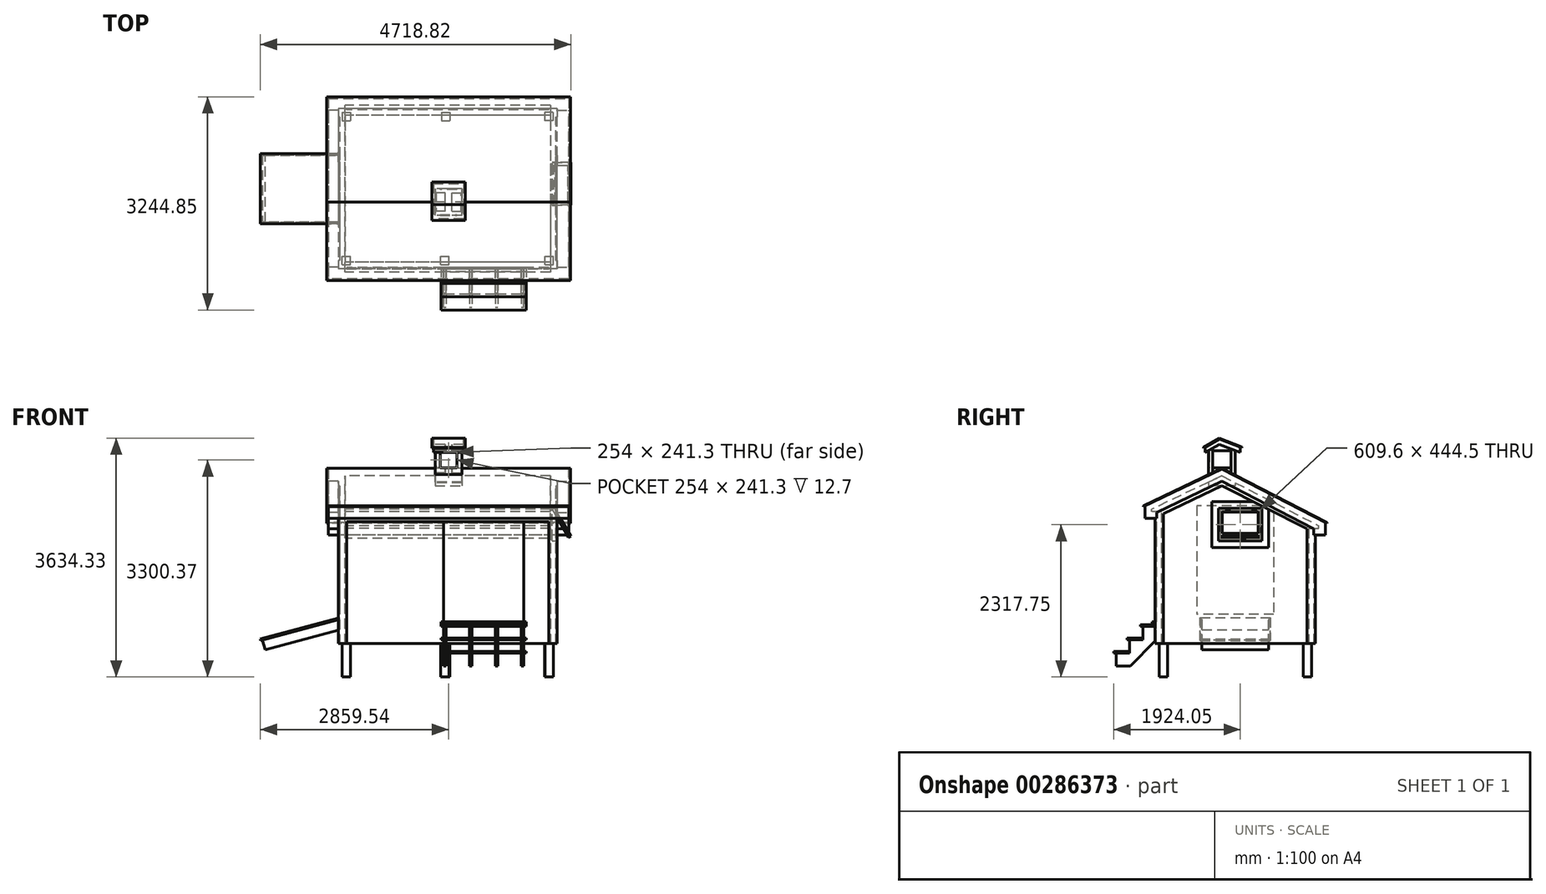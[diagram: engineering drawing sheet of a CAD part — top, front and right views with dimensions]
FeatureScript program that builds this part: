
annotation { "Feature Type Name" : "Feature", "Feature Type Description" : "" }
export const myFeature = defineFeature(function(context is Context, id is Id, definition is map)
    precondition{}
    {
        {
            var Q0;
            Q0=qCreatedBy(makeId("Right.planeOp"),FACE);
            var sketch = newSketch(context, id + "F0", { "sketchPlane" : qUnion([Q0])});
            skLineSegment(sketch, "E0", {"start": v(-152.4, 1905) * mm, "end": v(-152.4, 2108.2) * mm});
            skLineSegment(sketch, "E1", {"start": v(-152.4, 2108.2) * mm, "end": v(1016, 2667) * mm});
            skLineSegment(sketch, "E2", {"start": v(1016, 2667) * mm, "end": v(2590.8, 1854.2) * mm});
            skLineSegment(sketch, "E3", {"start": v(2590.8, 1854.2) * mm, "end": v(2590.8, 1651) * mm});
            skLineSegment(sketch, "E4", {"start": v(2590.8, 1651) * mm, "end": v(2438.4, 1651) * mm});
            skLineSegment(sketch, "E5", {"start": v(2438.4, 1651) * mm, "end": v(2438.4, 0) * mm});
            skLineSegment(sketch, "E6", {"start": v(2438.4, 0) * mm, "end": v(0, 0) * mm});
            skLineSegment(sketch, "E7", {"start": v(0, 0) * mm, "end": v(0, 1905) * mm});
            skLineSegment(sketch, "E8", {"start": v(0, 1905) * mm, "end": v(-152.4, 1905) * mm});
            skSolve(sketch);
        }
        {
            var Q0;
            Q0 = qSketchRegion(id + "F0", true);
            extrude(context, id + "F1", {"entities" : qUnion([Q0]), "depth" : 3657.6 * mm});
        }
        {
            var Q0;
            Q0=makeQuery(id+"F1.opExtrude","CAP_FACE",FACE,{"disambiguationData":[OSD([sQuery(id+"F0.wireOp",EDGE,"E0"),sQuery(id+"F0.wireOp",EDGE,"E1"),sQuery(id+"F0.wireOp",EDGE,"E2"),sQuery(id+"F0.wireOp",EDGE,"E3"),sQuery(id+"F0.wireOp",EDGE,"E4"),sQuery(id+"F0.wireOp",EDGE,"E5"),sQuery(id+"F0.wireOp",EDGE,"E6"),sQuery(id+"F0.wireOp",EDGE,"E7"),sQuery(id+"F0.wireOp",EDGE,"E8")])],"isStart":false});
            var sketch = newSketch(context, id + "F2", { "sketchPlane" : qUnion([Q0])});
            skLineSegment(sketch, "E9", {"start": v(0, 1905) * mm, "end": v(25.4, 1905) * mm});
            skLineSegment(sketch, "E10", {"start": v(25.4, 1905) * mm, "end": v(25.4, 1996.15) * mm});
            skLineSegment(sketch, "E11", {"start": v(25.4, 1996.15) * mm, "end": v(1016, 2469.91) * mm});
            skLineSegment(sketch, "E12", {"start": v(1016, 2469.91) * mm, "end": v(2413, 1748.88) * mm});
            skLineSegment(sketch, "E13", {"start": v(2413, 1748.88) * mm, "end": v(2413, 1651) * mm});
            skLineSegment(sketch, "E14", {"start": v(2413, 1651) * mm, "end": v(2438.4, 1651) * mm});
            skSolve(sketch);
        }
        {
            var Q0;
            Q0=makeQuery(id+"F2.imprint","IMPRINT",FACE,{"disambiguationData":[TD([[makeQuery(id+"F2.imprint","IMPRINT",EDGE,{"derivedFrom":sQuery(id+"F2.wireOp",EDGE,"E9")}),-1.0]])]});
            extrude(context, id + "F3", {"entities" : qUnion([Q0]), "operationType" : NewBodyOperationType.REMOVE, "oppositeDirection" : true, "depth" : 177.8 * mm});
        }
        {
            var Q0;
            Q0=makeQuery(id+"F1.opExtrude","CAP_FACE",FACE,{"disambiguationData":[OSD([sQuery(id+"F0.wireOp",EDGE,"E0"),sQuery(id+"F0.wireOp",EDGE,"E1"),sQuery(id+"F0.wireOp",EDGE,"E2"),sQuery(id+"F0.wireOp",EDGE,"E3"),sQuery(id+"F0.wireOp",EDGE,"E4"),sQuery(id+"F0.wireOp",EDGE,"E5"),sQuery(id+"F0.wireOp",EDGE,"E6"),sQuery(id+"F0.wireOp",EDGE,"E7"),sQuery(id+"F0.wireOp",EDGE,"E8")])],"isStart":true});
            var sketch = newSketch(context, id + "F4", { "sketchPlane" : qUnion([Q0])});
            skLineSegment(sketch, "E15.0.0", {"start": v(-2438.4, 1651) * mm, "end": v(-2413, 1651) * mm});
            skLineSegment(sketch, "E15.0.1", {"start": v(-2413, 1651) * mm, "end": v(-2413, 1748.88) * mm});
            skLineSegment(sketch, "E15.0.2", {"start": v(-2413, 1748.88) * mm, "end": v(-1016, 2469.91) * mm});
            skLineSegment(sketch, "E15.0.3", {"start": v(-1016, 2469.91) * mm, "end": v(-25.4, 1996.15) * mm});
            skLineSegment(sketch, "E15.0.4", {"start": v(-25.4, 1996.15) * mm, "end": v(-25.4, 1905) * mm});
            skLineSegment(sketch, "E15.0.5", {"start": v(-25.4, 1905) * mm, "end": v(0, 1905) * mm});
            skLineSegment(sketch, "E15.0.6", {"start": v(0, 1905) * mm, "end": v(0, 0) * mm});
            skLineSegment(sketch, "E15.0.7", {"start": v(0, 0) * mm, "end": v(-2438.4, 0) * mm});
            skLineSegment(sketch, "E15.0.8", {"start": v(-2438.4, 0) * mm, "end": v(-2438.4, 1651) * mm});
            skSolve(sketch);
        }
        {
            var Q0;
            Q0 = qSketchRegion(id + "F4", true);
            extrude(context, id + "F5", {"entities" : qUnion([Q0]), "operationType" : NewBodyOperationType.REMOVE, "oppositeDirection" : true, "depth" : 152.4 * mm});
        }
        {
            var Q0;
            Q0=makeQuery(id+"F1.opExtrude","SWEPT_FACE",FACE,{"disambiguationData":[OSD([sQuery(id+"F0.wireOp",EDGE,"E6")])]});
            shell(context, id + "F6", {"entities" : qUnion([Q0]), "thickness" : 101.6 * mm});
        }
        {
            var Q0;
            Q0=makeQuery(id+"F3.boolean.opBoolean","COPY",FACE,{"derivedFrom":makeQuery(id+"F3.opExtrude","CAP_FACE",FACE,{"disambiguationData":[OSD([sQuery(id+"F0.wireOp",EDGE,"E5"),sQuery(id+"F0.wireOp",EDGE,"E6"),sQuery(id+"F0.wireOp",EDGE,"E7"),sQuery(id+"F2.wireOp",EDGE,"E9"),sQuery(id+"F2.wireOp",EDGE,"E10"),sQuery(id+"F2.wireOp",EDGE,"E11"),sQuery(id+"F2.wireOp",EDGE,"E12"),sQuery(id+"F2.wireOp",EDGE,"E13"),sQuery(id+"F2.wireOp",EDGE,"E14")])],"isStart":false})});
            var sketch = newSketch(context, id + "F7", { "sketchPlane" : qUnion([Q0])});
            skLineSegment(sketch, "E16", {"start": v(127, 0) * mm, "end": v(127, 1974.35) * mm});
            skLineSegment(sketch, "E17", {"start": v(127, 1974.35) * mm, "end": v(1016, 2399.52) * mm});
            skLineSegment(sketch, "E18", {"start": v(1016, 2399.52) * mm, "end": v(2311.4, 1748.88) * mm});
            skLineSegment(sketch, "E19", {"start": v(2311.4, 1748.88) * mm, "end": v(2311.4, 0) * mm});
            skSolve(sketch);
        }
        {
            var Q0;
            {var subQ1=sQuery(id+"F7.wireOp",EDGE,"E16");Q0=makeQuery(id+"F7.imprint","IMPRINT",FACE,{"disambiguationData":[TD([[makeQuery(id+"F7.imprint","IMPRINT",EDGE,{"derivedFrom":subQ1}),-1.0]])]});}
            extrude(context, id + "F8", {"entities" : qUnion([Q0]), "operationType" : NewBodyOperationType.REMOVE, "oppositeDirection" : true, "depth" : 19.05 * mm});
        }
        {
            var Q0;
            Q0=makeQuery(id+"F5.boolean.opBoolean","COPY",FACE,{"derivedFrom":makeQuery(id+"F5.opExtrude","CAP_FACE",FACE,{"disambiguationData":[OSD([sQuery(id+"F4.wireOp",EDGE,"E15.0.0"),sQuery(id+"F4.wireOp",EDGE,"E15.0.1"),sQuery(id+"F4.wireOp",EDGE,"E15.0.2"),sQuery(id+"F4.wireOp",EDGE,"E15.0.3"),sQuery(id+"F4.wireOp",EDGE,"E15.0.4"),sQuery(id+"F4.wireOp",EDGE,"E15.0.5"),sQuery(id+"F4.wireOp",EDGE,"E15.0.6"),sQuery(id+"F4.wireOp",EDGE,"E15.0.7"),sQuery(id+"F4.wireOp",EDGE,"E15.0.8")])],"isStart":false})});
            var sketch = newSketch(context, id + "F9", { "sketchPlane" : qUnion([Q0])});
            skLineSegment(sketch, "E20.0.0", {"start": v(-2311.4, 0) * mm, "end": v(-2311.4, 1748.88) * mm});
            skLineSegment(sketch, "E20.0.1", {"start": v(-2311.4, 1748.88) * mm, "end": v(-1016, 2399.52) * mm});
            skLineSegment(sketch, "E20.0.2", {"start": v(-1016, 2399.52) * mm, "end": v(-127, 1974.35) * mm});
            skLineSegment(sketch, "E20.0.3", {"start": v(-127, 1974.35) * mm, "end": v(-127, 0) * mm});
            skLineSegment(sketch, "E20.0.4", {"start": v(-127, 0) * mm, "end": v(-2311.4, 0) * mm});
            skSolve(sketch);
        }
        {
            var Q0;
            Q0 = qSketchRegion(id + "F9", true);
            extrude(context, id + "F10", {"entities" : qUnion([Q0]), "operationType" : NewBodyOperationType.REMOVE, "oppositeDirection" : true, "depth" : 19.05 * mm});
        }
        {
            var Q0;
            Q0=makeQuery(id+"F1.opExtrude","SWEPT_FACE",FACE,{"disambiguationData":[OSD([sQuery(id+"F0.wireOp",EDGE,"E7")])]});
            var sketch = newSketch(context, id + "F11", { "sketchPlane" : qUnion([Q0])});
            skLineSegment(sketch, "E21", {"start": v(279.4, 0) * mm, "end": v(279.4, 1854.2) * mm});
            skLineSegment(sketch, "E22", {"start": v(279.4, 1854.2) * mm, "end": v(3352.8, 1854.2) * mm});
            skLineSegment(sketch, "E23", {"start": v(3352.8, 1854.2) * mm, "end": v(3352.8, 0) * mm});
            skSolve(sketch);
        }
        {
            var Q0;
            {var subQ0=sQuery(id+"F11.wireOp",EDGE,"E21");Q0=makeQuery(id+"F11.imprint","IMPRINT",FACE,{"disambiguationData":[TD([[makeQuery(id+"F11.imprint","IMPRINT",EDGE,{"derivedFrom":subQ0}),-1.0]])]});}
            extrude(context, id + "F12", {"entities" : qUnion([Q0]), "operationType" : NewBodyOperationType.REMOVE, "oppositeDirection" : true, "depth" : 19.05 * mm});
        }
        {
            var Q0;
            Q0=makeQuery(id+"F1.opExtrude","SWEPT_FACE",FACE,{"disambiguationData":[OSD([sQuery(id+"F0.wireOp",EDGE,"E5")])]});
            var sketch = newSketch(context, id + "F13", { "sketchPlane" : qUnion([Q0])});
            skLineSegment(sketch, "E24", {"start": v(-3352.8, 0) * mm, "end": v(-3352.8, 1600.2) * mm});
            skLineSegment(sketch, "E25", {"start": v(-3352.8, 1600.2) * mm, "end": v(-279.4, 1600.2) * mm});
            skLineSegment(sketch, "E26", {"start": v(-279.4, 1600.2) * mm, "end": v(-279.4, 0) * mm});
            skSolve(sketch);
        }
        {
            var Q0;
            {var subQ0=sQuery(id+"F13.wireOp",EDGE,"E24");Q0=makeQuery(id+"F13.imprint","IMPRINT",FACE,{"disambiguationData":[TD([[makeQuery(id+"F13.imprint","IMPRINT",EDGE,{"derivedFrom":subQ0}),-1.0]])]});}
            extrude(context, id + "F14", {"entities" : qUnion([Q0]), "operationType" : NewBodyOperationType.REMOVE, "oppositeDirection" : true, "depth" : 19.05 * mm});
        }
        {
            var Q0;
            Q0=makeQuery(id+"F1.opExtrude","CAP_FACE",FACE,{"disambiguationData":[OSD([sQuery(id+"F0.wireOp",EDGE,"E0"),sQuery(id+"F0.wireOp",EDGE,"E1"),sQuery(id+"F0.wireOp",EDGE,"E2"),sQuery(id+"F0.wireOp",EDGE,"E3"),sQuery(id+"F0.wireOp",EDGE,"E4"),sQuery(id+"F0.wireOp",EDGE,"E5"),sQuery(id+"F0.wireOp",EDGE,"E6"),sQuery(id+"F0.wireOp",EDGE,"E7"),sQuery(id+"F0.wireOp",EDGE,"E8")])],"isStart":false});
            var sketch = newSketch(context, id + "F15", { "sketchPlane" : qUnion([Q0])});
            skLineSegment(sketch, "E27", {"start": v(1016, 2667) * mm, "end": v(-177.8, 2096.05) * mm});
            skLineSegment(sketch, "E28", {"start": v(-177.8, 2096.05) * mm, "end": v(-177.8, 2081.97) * mm});
            skLineSegment(sketch, "E29", {"start": v(-177.8, 2081.97) * mm, "end": v(1016, 2652.92) * mm});
            skLineSegment(sketch, "E30", {"start": v(1016, 2652.92) * mm, "end": v(2616.2, 1827.01) * mm});
            skLineSegment(sketch, "E31", {"start": v(2616.2, 1827.01) * mm, "end": v(2616.2, 1841.1) * mm});
            skLineSegment(sketch, "E32", {"start": v(2616.2, 1841.1) * mm, "end": v(1016, 2667) * mm});
            skSolve(sketch);
        }
        {
            var Q0;
            Q0 = qSketchRegion(id + "F15", true);
            extrude(context, id + "F16", {"entities" : qUnion([Q0]), "operationType" : NewBodyOperationType.ADD, "depth" : 25.4 * mm, "hasSecondDirection" : true, "secondDirectionOppositeDirection" : true, "secondDirectionDepth" : 3683 * mm});
        }
        {
            var Q0;
            Q0=makeQuery(id+"F8.boolean.opBoolean","COPY",FACE,{"derivedFrom":makeQuery(id+"F8.opExtrude","CAP_FACE",FACE,{"disambiguationData":[OSD([sQuery(id+"F0.wireOp",EDGE,"E6"),sQuery(id+"F7.wireOp",EDGE,"E16"),sQuery(id+"F7.wireOp",EDGE,"E17"),sQuery(id+"F7.wireOp",EDGE,"E18"),sQuery(id+"F7.wireOp",EDGE,"E19")])],"isStart":false})});
            var sketch = newSketch(context, id + "F17", { "sketchPlane" : qUnion([Q0])});
            skLineSegment(sketch, "E33.bottom", {"start": v(863.6, 2159) * mm, "end": v(1727.2, 2159) * mm});
            skLineSegment(sketch, "E33.top", {"start": v(863.6, 1460.5) * mm, "end": v(1727.2, 1460.5) * mm});
            skLineSegment(sketch, "E33.left", {"start": v(863.6, 2159) * mm, "end": v(863.6, 1460.5) * mm});
            skLineSegment(sketch, "E33.right", {"start": v(1727.2, 2159) * mm, "end": v(1727.2, 1460.5) * mm});
            skSolve(sketch);
        }
        {
            var Q0;
            Q0 = qSketchRegion(id + "F17", true);
            extrude(context, id + "F18", {"entities" : qUnion([Q0]), "operationType" : NewBodyOperationType.ADD, "depth" : 17.78 * mm});
        }
        {
            var Q0;
            Q0=makeQuery(id+"F18.opExtrude","CAP_FACE",FACE,{"disambiguationData":[OSD([sQuery(id+"F17.wireOp",EDGE,"E33.bottom"),sQuery(id+"F17.wireOp",EDGE,"E33.top"),sQuery(id+"F17.wireOp",EDGE,"E33.left"),sQuery(id+"F17.wireOp",EDGE,"E33.right")])],"isStart":false});
            var sketch = newSketch(context, id + "F19", { "sketchPlane" : qUnion([Q0])});
            skLineSegment(sketch, "E34.1", {"start": v(1625.6, 1562.1) * mm, "end": v(1625.6, 2057.4) * mm});
            skLineSegment(sketch, "E34.2", {"start": v(1625.6, 2057.4) * mm, "end": v(965.2, 2057.4) * mm});
            skLineSegment(sketch, "E34.3", {"start": v(965.2, 2057.4) * mm, "end": v(965.2, 1562.1) * mm});
            skLineSegment(sketch, "E34.4", {"start": v(965.2, 1562.1) * mm, "end": v(1625.6, 1562.1) * mm});
            skSolve(sketch);
        }
        {
            var Q0;
            Q0 = qSketchRegion(id + "F19", true);
            extrude(context, id + "F20", {"entities" : qUnion([Q0]), "operationType" : NewBodyOperationType.REMOVE, "oppositeDirection" : true, "depth" : 76.2 * mm});
        }
        {
            var Q0;
            Q0=makeQuery(id+"F12.boolean.opBoolean","COPY",FACE,{"derivedFrom":makeQuery(id+"F12.opExtrude","CAP_FACE",FACE,{"disambiguationData":[OSD([sQuery(id+"F0.wireOp",EDGE,"E6"),sQuery(id+"F0.wireOp",EDGE,"E7"),sQuery(id+"F11.wireOp",EDGE,"E21"),sQuery(id+"F11.wireOp",EDGE,"E22"),sQuery(id+"F11.wireOp",EDGE,"E23")])],"isStart":false})});
            var sketch = newSketch(context, id + "F21", { "sketchPlane" : qUnion([Q0])});
            skLineSegment(sketch, "E35.bottom", {"start": v(1752.6, 1854.2) * mm, "end": v(2971.8, 1854.2) * mm});
            skLineSegment(sketch, "E35.top", {"start": v(1752.6, 330.2) * mm, "end": v(2971.8, 330.2) * mm});
            skLineSegment(sketch, "E35.left", {"start": v(1752.6, 1854.2) * mm, "end": v(1752.6, 330.2) * mm});
            skLineSegment(sketch, "E35.right", {"start": v(2971.8, 1854.2) * mm, "end": v(2971.8, 330.2) * mm});
            skSolve(sketch);
        }
        {
            var Q0;
            Q0 = qSketchRegion(id + "F21", true);
            extrude(context, id + "F22", {"entities" : qUnion([Q0]), "operationType" : NewBodyOperationType.ADD, "depth" : 17.78 * mm});
        }
        {
            var Q0;
            Q0=makeQuery(id+"F20.boolean.opBoolean","COPY",FACE,{"derivedFrom":makeQuery(id+"F20.opExtrude","CAP_FACE",FACE,{"disambiguationData":[OSD([sQuery(id+"F19.wireOp",EDGE,"E34.1"),sQuery(id+"F19.wireOp",EDGE,"E34.2"),sQuery(id+"F19.wireOp",EDGE,"E34.3"),sQuery(id+"F19.wireOp",EDGE,"E34.4")])],"isStart":false})});
            var sketch = newSketch(context, id + "F23", { "sketchPlane" : qUnion([Q0])});
            skLineSegment(sketch, "E36.0", {"start": v(990.6, 2032) * mm, "end": v(990.6, 1587.5) * mm});
            skLineSegment(sketch, "E36.1", {"start": v(1600.2, 2032) * mm, "end": v(990.6, 2032) * mm});
            skLineSegment(sketch, "E36.2", {"start": v(1600.2, 1587.5) * mm, "end": v(1600.2, 2032) * mm});
            skLineSegment(sketch, "E36.3", {"start": v(990.6, 1587.5) * mm, "end": v(1600.2, 1587.5) * mm});
            skSolve(sketch);
        }
        {
            var Q0;
            Q0 = qSketchRegion(id + "F23", true);
            extrude(context, id + "F24", {"entities" : qUnion([Q0]), "operationType" : NewBodyOperationType.REMOVE, "oppositeDirection" : true, "depth" : 76.2 * mm});
        }
        {
            var Q0;
            Q0=makeQuery(id+"F10.boolean.opBoolean","COPY",FACE,{"derivedFrom":makeQuery(id+"F10.opExtrude","CAP_FACE",FACE,{"disambiguationData":[OSD([sQuery(id+"F9.wireOp",EDGE,"E20.0.0"),sQuery(id+"F9.wireOp",EDGE,"E20.0.1"),sQuery(id+"F9.wireOp",EDGE,"E20.0.2"),sQuery(id+"F9.wireOp",EDGE,"E20.0.3"),sQuery(id+"F9.wireOp",EDGE,"E20.0.4")])],"isStart":false})});
            var sketch = newSketch(context, id + "F25", { "sketchPlane" : qUnion([Q0])});
            skLineSegment(sketch, "E37.bottom", {"start": v(-1803.4, 2094.72) * mm, "end": v(-635, 2094.72) * mm});
            skLineSegment(sketch, "E37.top", {"start": v(-1803.4, 443.72) * mm, "end": v(-635, 443.72) * mm});
            skLineSegment(sketch, "E37.left", {"start": v(-1803.4, 2094.72) * mm, "end": v(-1803.4, 443.72) * mm});
            skLineSegment(sketch, "E37.right", {"start": v(-635, 2094.72) * mm, "end": v(-635, 443.72) * mm});
            skSolve(sketch);
        }
        {
            var Q0;
            Q0 = qSketchRegion(id + "F25", true);
            extrude(context, id + "F26", {"entities" : qUnion([Q0]), "operationType" : NewBodyOperationType.ADD, "depth" : 17.78 * mm});
        }
        {
            var Q0;
            Q0=makeQuery(id+"F26.opExtrude","CAP_EDGE",EDGE,{"disambiguationData":[OSD([sQuery(id+"F25.wireOp",EDGE,"E37.top")])],"isStart":false});
            cPoint(context, id + "F27", {"entities" : qUnion([Q0]), "parameter" : 0.5});
        }
        {
            var Q0;
            Q0=makeQuery(id+"F12.boolean.opBoolean","COPY",FACE,{"derivedFrom":makeQuery(id+"F12.opExtrude","CAP_FACE",FACE,{"disambiguationData":[OSD([sQuery(id+"F0.wireOp",EDGE,"E6"),sQuery(id+"F0.wireOp",EDGE,"E7"),sQuery(id+"F11.wireOp",EDGE,"E21"),sQuery(id+"F11.wireOp",EDGE,"E22"),sQuery(id+"F11.wireOp",EDGE,"E23")])],"isStart":false})});
            var Q1;
            Q1 = qCreatedBy(id + "F27" ,VERTEX);
            cPlane(context, id + "F28", {"entities" : qUnion([Q0, Q1]), "cplaneType" : CPlaneType.PLANE_POINT, "offset" : 25.4 * mm, "width" : 152.4 * mm, "height" : 152.4 * mm});
        }
        {
            var Q0;
            Q0=qCreatedBy(id+"F28.planeOp",FACE);
            var sketch = newSketch(context, id + "F29", { "sketchPlane" : qUnion([Q0])});
            skLineSegment(sketch, "E38", {"start": v(171.45, 392.92) * mm, "end": v(-1006.2, 77.37) * mm});
            skLineSegment(sketch, "E39", {"start": v(-1006.2, 77.37) * mm, "end": v(-960.19, -94.37) * mm});
            skLineSegment(sketch, "E40", {"start": v(-960.19, -94.37) * mm, "end": v(171.45, 208.85) * mm});
            skLineSegment(sketch, "E41", {"start": v(171.45, 208.85) * mm, "end": v(171.45, 392.92) * mm});
            skSolve(sketch);
        }
        {
            var Q0;
            Q0 = qSketchRegion(id + "F29", true);
            extrude(context, id + "F30", {"entities" : qUnion([Q0]), "operationType" : NewBodyOperationType.ADD, "endBound" : BoundingType.SYMMETRIC, "depth" : 1016 * mm});
        }
        {
            var Q0;
            Q0=makeQuery(id+"F30.opExtrude","CAP_FACE",FACE,{"disambiguationData":[OSD([sQuery(id+"F29.wireOp",EDGE,"E38"),sQuery(id+"F29.wireOp",EDGE,"E39"),sQuery(id+"F29.wireOp",EDGE,"E40"),sQuery(id+"F29.wireOp",EDGE,"E41")])],"isStart":false});
            var sketch = newSketch(context, id + "F31", { "sketchPlane" : qUnion([Q0])});
            skLineSegment(sketch, "E42", {"start": v(171.45, 392.92) * mm, "end": v(-1030.74, 70.8) * mm});
            skLineSegment(sketch, "E43", {"start": v(-1030.74, 70.8) * mm, "end": v(-1024.17, 46.26) * mm});
            skLineSegment(sketch, "E44", {"start": v(-1024.17, 46.26) * mm, "end": v(171.45, 366.63) * mm});
            skLineSegment(sketch, "E45", {"start": v(171.45, 366.63) * mm, "end": v(171.45, 392.92) * mm});
            skSolve(sketch);
        }
        {
            var Q0;
            Q0 = qSketchRegion(id + "F31", true);
            extrude(context, id + "F32", {"entities" : qUnion([Q0]), "operationType" : NewBodyOperationType.ADD, "depth" : 25.4 * mm, "hasSecondDirection" : true, "secondDirectionOppositeDirection" : true, "secondDirectionDepth" : 1041.4 * mm});
        }
        {
            var Q0;
            Q0=makeQuery(id+"F1.opExtrude","SWEPT_FACE",FACE,{"disambiguationData":[OSD([sQuery(id+"F0.wireOp",EDGE,"E6")])]});
            var Q1;
            Q1=makeQuery(id+"F10.boolean.opBoolean","COPY",VERTEX,{"derivedFrom":makeQuery(id+"F10.opExtrude","CAP_VERTEX",VERTEX,{"disambiguationData":[OSD([sQuery(id+"F9.wireOp",EDGE,"E20.0.1"),sQuery(id+"F9.wireOp",EDGE,"E20.0.2")])],"isStart":false})});
            cPlane(context, id + "F33", {"entities" : qUnion([Q0, Q1]), "cplaneType" : CPlaneType.PLANE_POINT, "offset" : 25.4 * mm, "width" : 152.4 * mm, "height" : 152.4 * mm});
        }
        {
            var Q0;
            Q0=qCreatedBy(id+"F33.planeOp",FACE);
            var sketch = newSketch(context, id + "F34", { "sketchPlane" : qUnion([Q0])});
            skLineSegment(sketch, "E46.bottom", {"start": v(1625.6, -1219.2) * mm, "end": v(2032, -1219.2) * mm});
            skLineSegment(sketch, "E46.top", {"start": v(1625.6, -812.8) * mm, "end": v(2032, -812.8) * mm});
            skLineSegment(sketch, "E46.left", {"start": v(1625.6, -1219.2) * mm, "end": v(1625.6, -812.8) * mm});
            skLineSegment(sketch, "E46.right", {"start": v(2032, -1219.2) * mm, "end": v(2032, -812.8) * mm});
            skLineSegment(sketch, "E47", {"start": v(2032, -1016) * mm, "end": v(1378.54, -1016) * mm, "construction": true});
            skPoint(sketch, "E47.endSnap0", {"position": v(1625.6, -1016) * mm});
            skLineSegment(sketch, "E48", {"start": v(1828.8, -1219.2) * mm, "end": v(1828.8, -1016) * mm, "construction": true});
            skPoint(sketch, "E48.endSnap0", {"position": v(1705.27, -1016) * mm});
            skSolve(sketch);
        }
        {
            var Q0;
            Q0 = qSketchRegion(id + "F34", true);
            extrude(context, id + "F35", {"entities" : qUnion([Q0]), "operationType" : NewBodyOperationType.ADD, "oppositeDirection" : true, "depth" : 632.46 * mm});
        }
        {
            var Q0;
            {var subQ2=sQuery(id+"F34.wireOp",EDGE,"E46.right");Q0=makeQuery(id+"F35.boolean.opBoolean","SPLIT",FACE,{"disambiguationData":[TD([makeQuery(id+"F1.opExtrude","SWEPT_FACE",FACE,{"disambiguationData":[OSD([sQuery(id+"F0.wireOp",EDGE,"E1")])]})])],"derivedFrom":makeQuery(id+"F35.opExtrude","SWEPT_FACE",FACE,{"disambiguationData":[OSD([subQ2])]})});}
            var sketch = newSketch(context, id + "F36", { "sketchPlane" : qUnion([Q0])});
            skLineSegment(sketch, "E49", {"start": v(762, 3002.65) * mm, "end": v(976.22, 3126.33) * mm});
            skLineSegment(sketch, "E50", {"start": v(976.22, 3126.33) * mm, "end": v(1294.73, 3002.65) * mm});
            skLineSegment(sketch, "E51", {"start": v(1294.73, 3002.65) * mm, "end": v(1294.73, 2907.29) * mm});
            skLineSegment(sketch, "E52", {"start": v(1294.73, 2907.29) * mm, "end": v(976.22, 3030.97) * mm});
            skLineSegment(sketch, "E53", {"start": v(976.22, 3030.97) * mm, "end": v(762, 2907.29) * mm});
            skLineSegment(sketch, "E54", {"start": v(762, 2907.29) * mm, "end": v(762, 3002.65) * mm});
            skSolve(sketch);
        }
        {
            var Q0;
            Q0 = qSketchRegion(id + "F36", true);
            extrude(context, id + "F37", {"entities" : qUnion([Q0]), "operationType" : NewBodyOperationType.ADD, "depth" : 25.4 * mm, "hasSecondDirection" : true, "secondDirectionOppositeDirection" : true, "secondDirectionDepth" : 431.8 * mm});
        }
        {
            var Q0;
            Q0=makeQuery(id+"F37.opExtrude","CAP_FACE",FACE,{"disambiguationData":[OSD([sQuery(id+"F36.wireOp",EDGE,"E49"),sQuery(id+"F36.wireOp",EDGE,"E50"),sQuery(id+"F36.wireOp",EDGE,"E51"),sQuery(id+"F36.wireOp",EDGE,"E52"),sQuery(id+"F36.wireOp",EDGE,"E53"),sQuery(id+"F36.wireOp",EDGE,"E54")])],"isStart":false});
            var sketch = newSketch(context, id + "F38", { "sketchPlane" : qUnion([Q0])});
            skLineSegment(sketch, "E55", {"start": v(976.22, 3126.33) * mm, "end": v(736.6, 2987.99) * mm});
            skLineSegment(sketch, "E56", {"start": v(736.6, 2987.99) * mm, "end": v(736.6, 2974.37) * mm});
            skLineSegment(sketch, "E57", {"start": v(736.6, 2974.37) * mm, "end": v(976.22, 3112.7) * mm});
            skLineSegment(sketch, "E58", {"start": v(976.22, 3112.7) * mm, "end": v(1320.13, 2979.17) * mm});
            skLineSegment(sketch, "E59", {"start": v(976.22, 3126.33) * mm, "end": v(1320.13, 2992.8) * mm});
            skLineSegment(sketch, "E60", {"start": v(1320.13, 2992.8) * mm, "end": v(1320.13, 2979.17) * mm});
            skSolve(sketch);
        }
        {
            var Q0;
            Q0 = qSketchRegion(id + "F38", true);
            extrude(context, id + "F39", {"entities" : qUnion([Q0]), "operationType" : NewBodyOperationType.ADD, "depth" : 25.4 * mm, "hasSecondDirection" : true, "secondDirectionOppositeDirection" : true, "secondDirectionDepth" : 482.6 * mm});
        }
        {
            var Q0;
            {var subQ2=sQuery(id+"F34.wireOp",EDGE,"E46.right");Q0=makeQuery(id+"F35.boolean.opBoolean","SPLIT",FACE,{"disambiguationData":[TD([makeQuery(id+"F1.opExtrude","SWEPT_FACE",FACE,{"disambiguationData":[OSD([sQuery(id+"F0.wireOp",EDGE,"E1")])]})])],"derivedFrom":makeQuery(id+"F35.opExtrude","SWEPT_FACE",FACE,{"disambiguationData":[OSD([subQ2])]})});}
            var sketch = newSketch(context, id + "F40", { "sketchPlane" : qUnion([Q0])});
            skLineSegment(sketch, "E61.bottom", {"start": v(876.3, 2936.62) * mm, "end": v(1155.7, 2936.62) * mm});
            skLineSegment(sketch, "E61.top", {"start": v(876.3, 2676.6) * mm, "end": v(1155.7, 2676.6) * mm});
            skLineSegment(sketch, "E61.left", {"start": v(876.3, 2936.62) * mm, "end": v(876.3, 2676.6) * mm});
            skLineSegment(sketch, "E61.right", {"start": v(1155.7, 2936.62) * mm, "end": v(1155.7, 2676.6) * mm});
            skSolve(sketch);
        }
        {
            var Q0;
            Q0=makeQuery(id+"F40.imprint","IMPRINT",FACE,{"disambiguationData":[TD([[makeQuery(id+"F40.imprint","IMPRINT",EDGE,{"derivedFrom":sQuery(id+"F40.wireOp",EDGE,"E61.bottom")}),-1.0]])]});
            extrude(context, id + "F41", {"entities" : qUnion([Q0]), "operationType" : NewBodyOperationType.REMOVE, "oppositeDirection" : true, "depth" : 12.7 * mm});
        }
        {
            var Q0;
            {var subQ2=sQuery(id+"F34.wireOp",EDGE,"E46.left");Q0=makeQuery(id+"F35.boolean.opBoolean","SPLIT",FACE,{"disambiguationData":[TD([makeQuery(id+"F1.opExtrude","SWEPT_FACE",FACE,{"disambiguationData":[OSD([sQuery(id+"F0.wireOp",EDGE,"E1")])]})])],"derivedFrom":makeQuery(id+"F35.opExtrude","SWEPT_FACE",FACE,{"disambiguationData":[OSD([subQ2])]})});}
            var sketch = newSketch(context, id + "F42", { "sketchPlane" : qUnion([Q0])});
            skLineSegment(sketch, "E62.0.0", {"start": v(-876.3, 2936.62) * mm, "end": v(-876.3, 2676.6) * mm});
            skLineSegment(sketch, "E62.0.1", {"start": v(-876.3, 2676.6) * mm, "end": v(-1155.7, 2676.6) * mm});
            skLineSegment(sketch, "E62.0.2", {"start": v(-1155.7, 2676.6) * mm, "end": v(-1155.7, 2936.62) * mm});
            skLineSegment(sketch, "E62.0.3", {"start": v(-1155.7, 2936.62) * mm, "end": v(-876.3, 2936.62) * mm});
            skSolve(sketch);
        }
        {
            var Q0;
            Q0 = qSketchRegion(id + "F42", true);
            extrude(context, id + "F43", {"entities" : qUnion([Q0]), "operationType" : NewBodyOperationType.REMOVE, "oppositeDirection" : true, "depth" : 12.7 * mm});
        }
        {
            var Q0;
            {var subQ2=sQuery(id+"F34.wireOp",EDGE,"E46.right");Q0=makeQuery(id+"F35.boolean.opBoolean","SPLIT",FACE,{"disambiguationData":[TD([makeQuery(id+"F1.opExtrude","SWEPT_FACE",FACE,{"disambiguationData":[OSD([sQuery(id+"F0.wireOp",EDGE,"E1")])]})])],"derivedFrom":makeQuery(id+"F35.opExtrude","SWEPT_FACE",FACE,{"disambiguationData":[OSD([subQ2])]})});}
            var sketch = newSketch(context, id + "F44", { "sketchPlane" : qUnion([Q0])});
            skLineSegment(sketch, "E63", {"start": v(876.3, 2936.62) * mm, "end": v(876.3, 2973.28) * mm});
            skLineSegment(sketch, "E64", {"start": v(976.22, 3030.97) * mm, "end": v(1155.7, 2961.27) * mm});
            skLineSegment(sketch, "E65", {"start": v(1155.7, 2961.27) * mm, "end": v(1155.7, 2936.62) * mm});
            skLineSegment(sketch, "E66", {"start": v(876.3, 2676.6) * mm, "end": v(876.3, 2600.19) * mm});
            skLineSegment(sketch, "E67", {"start": v(876.3, 2600.19) * mm, "end": v(1016, 2667) * mm});
            skLineSegment(sketch, "E68", {"start": v(1016, 2667) * mm, "end": v(1155.7, 2594.9) * mm});
            skLineSegment(sketch, "E69", {"start": v(1155.7, 2594.9) * mm, "end": v(1155.7, 2676.6) * mm});
            skSolve(sketch);
        }
        {
            var Q0;
            {var subQ1=sQuery(id+"F44.wireOp",EDGE,"E63");Q0=makeQuery(id+"F44.imprint","IMPRINT",FACE,{"disambiguationData":[TD([[makeQuery(id+"F44.imprint","IMPRINT",EDGE,{"derivedFrom":subQ1}),-1.0]])]});}
            var Q1;
            Q1=makeQuery(id+"F44.imprint","IMPRINT",FACE,{"disambiguationData":[TD([[makeQuery(id+"F44.imprint","IMPRINT",EDGE,{"derivedFrom":sQuery(id+"F44.wireOp",EDGE,"E66")}),1.0]])]});
            extrude(context, id + "F45", {"entities" : qUnion([Q0, Q1]), "operationType" : NewBodyOperationType.REMOVE, "oppositeDirection" : true, "depth" : 152.4 * mm});
        }
        {
            var Q0;
            {var subQ2=sQuery(id+"F34.wireOp",EDGE,"E46.left");Q0=makeQuery(id+"F35.boolean.opBoolean","SPLIT",FACE,{"disambiguationData":[TD([makeQuery(id+"F1.opExtrude","SWEPT_FACE",FACE,{"disambiguationData":[OSD([sQuery(id+"F0.wireOp",EDGE,"E1")])]})])],"derivedFrom":makeQuery(id+"F35.opExtrude","SWEPT_FACE",FACE,{"disambiguationData":[OSD([subQ2])]})});}
            var sketch = newSketch(context, id + "F46", { "sketchPlane" : qUnion([Q0])});
            skLineSegment(sketch, "E70.0.0", {"start": v(-1155.7, 2936.62) * mm, "end": v(-1155.7, 2961.27) * mm});
            skLineSegment(sketch, "E70.0.1", {"start": v(-1155.7, 2961.27) * mm, "end": v(-976.22, 3030.97) * mm});
            skLineSegment(sketch, "E70.0.2", {"start": v(-976.22, 3030.97) * mm, "end": v(-876.3, 2973.28) * mm});
            skLineSegment(sketch, "E70.0.3", {"start": v(-876.3, 2973.28) * mm, "end": v(-876.3, 2936.62) * mm});
            skLineSegment(sketch, "E70.0.4", {"start": v(-876.3, 2936.62) * mm, "end": v(-1155.7, 2936.62) * mm});
            skLineSegment(sketch, "E71.0.0", {"start": v(-1016, 2667) * mm, "end": v(-1155.7, 2594.9) * mm});
            skLineSegment(sketch, "E71.0.1", {"start": v(-1155.7, 2594.9) * mm, "end": v(-1155.7, 2676.6) * mm});
            skLineSegment(sketch, "E71.0.2", {"start": v(-1155.7, 2676.6) * mm, "end": v(-876.3, 2676.6) * mm});
            skLineSegment(sketch, "E71.0.3", {"start": v(-876.3, 2676.6) * mm, "end": v(-876.3, 2600.19) * mm});
            skLineSegment(sketch, "E71.0.4", {"start": v(-876.3, 2600.19) * mm, "end": v(-1016, 2667) * mm});
            skSolve(sketch);
        }
        {
            var Q0;
            Q0 = qSketchRegion(id + "F46", true);
            extrude(context, id + "F47", {"entities" : qUnion([Q0]), "operationType" : NewBodyOperationType.REMOVE, "oppositeDirection" : true, "depth" : 152.4 * mm});
        }
        {
            var Q0;
            {var subQ2=sQuery(id+"F34.wireOp",EDGE,"E46.top");Q0=makeQuery(id+"F35.boolean.opBoolean","SPLIT",FACE,{"disambiguationData":[TD([makeQuery(id+"F1.opExtrude","SWEPT_FACE",FACE,{"disambiguationData":[OSD([sQuery(id+"F0.wireOp",EDGE,"E1")])]})])],"derivedFrom":makeQuery(id+"F35.opExtrude","SWEPT_FACE",FACE,{"disambiguationData":[OSD([subQ2])]})});}
            var sketch = newSketch(context, id + "F48", { "sketchPlane" : qUnion([Q0])});
            skLineSegment(sketch, "E72.bottom", {"start": v(1701.8, 2913.02) * mm, "end": v(1955.8, 2913.02) * mm});
            skLineSegment(sketch, "E72.top", {"start": v(1701.8, 2671.72) * mm, "end": v(1955.8, 2671.72) * mm});
            skLineSegment(sketch, "E72.left", {"start": v(1701.8, 2913.02) * mm, "end": v(1701.8, 2671.72) * mm});
            skLineSegment(sketch, "E72.right", {"start": v(1955.8, 2913.02) * mm, "end": v(1955.8, 2671.72) * mm});
            skSolve(sketch);
        }
        {
            var Q0;
            Q0 = qSketchRegion(id + "F48", true);
            extrude(context, id + "F49", {"entities" : qUnion([Q0]), "operationType" : NewBodyOperationType.REMOVE, "oppositeDirection" : true, "depth" : 12.7 * mm});
        }
        {
            var Q0;
            {var subQ2=sQuery(id+"F34.wireOp",EDGE,"E46.bottom");Q0=makeQuery(id+"F35.boolean.opBoolean","SPLIT",FACE,{"disambiguationData":[TD([makeQuery(id+"F1.opExtrude","SWEPT_FACE",FACE,{"disambiguationData":[OSD([sQuery(id+"F0.wireOp",EDGE,"E2")])]})])],"derivedFrom":makeQuery(id+"F35.opExtrude","SWEPT_FACE",FACE,{"disambiguationData":[OSD([subQ2])]})});}
            var sketch = newSketch(context, id + "F50", { "sketchPlane" : qUnion([Q0])});
            skLineSegment(sketch, "E73.0.0", {"start": v(-1701.8, 2913.02) * mm, "end": v(-1701.8, 2671.72) * mm});
            skLineSegment(sketch, "E73.0.1", {"start": v(-1701.8, 2671.72) * mm, "end": v(-1955.8, 2671.72) * mm});
            skLineSegment(sketch, "E73.0.2", {"start": v(-1955.8, 2671.72) * mm, "end": v(-1955.8, 2913.02) * mm});
            skLineSegment(sketch, "E73.0.3", {"start": v(-1955.8, 2913.02) * mm, "end": v(-1701.8, 2913.02) * mm});
            skSolve(sketch);
        }
        {
            var Q0;
            Q0 = qSketchRegion(id + "F50", true);
            extrude(context, id + "F51", {"entities" : qUnion([Q0]), "operationType" : NewBodyOperationType.REMOVE, "oppositeDirection" : true, "depth" : 12.7 * mm});
        }
        {
            var Q0;
            Q0=makeQuery(id+"F22.opExtrude","CAP_EDGE",EDGE,{"disambiguationData":[OSD([sQuery(id+"F21.wireOp",EDGE,"E35.top")])],"isStart":false});
            cPoint(context, id + "F52", {"entities" : qUnion([Q0]), "parameter" : 0.5});
        }
        {
            var Q0;
            Q0=makeQuery(id+"F3.boolean.opBoolean","COPY",FACE,{"derivedFrom":makeQuery(id+"F3.opExtrude","CAP_FACE",FACE,{"disambiguationData":[OSD([sQuery(id+"F0.wireOp",EDGE,"E5"),sQuery(id+"F0.wireOp",EDGE,"E6"),sQuery(id+"F0.wireOp",EDGE,"E7"),sQuery(id+"F2.wireOp",EDGE,"E9"),sQuery(id+"F2.wireOp",EDGE,"E10"),sQuery(id+"F2.wireOp",EDGE,"E11"),sQuery(id+"F2.wireOp",EDGE,"E12"),sQuery(id+"F2.wireOp",EDGE,"E13"),sQuery(id+"F2.wireOp",EDGE,"E14")])],"isStart":false})});
            var Q1;
            Q1 = qCreatedBy(id + "F52" ,VERTEX);
            cPlane(context, id + "F53", {"entities" : qUnion([Q0, Q1]), "cplaneType" : CPlaneType.PLANE_POINT, "offset" : 25.4 * mm, "width" : 152.4 * mm, "height" : 152.4 * mm});
        }
        {
            var Q0;
            Q0=qCreatedBy(id+"F53.planeOp",FACE);
            var sketch = newSketch(context, id + "F54", { "sketchPlane" : qUnion([Q0])});
            skLineSegment(sketch, "E74", {"start": v(19.05, 259.08) * mm, "end": v(-184.15, 259.08) * mm});
            skLineSegment(sketch, "E75", {"start": v(-184.15, 259.08) * mm, "end": v(-184.15, 55.88) * mm});
            skLineSegment(sketch, "E76", {"start": v(-184.15, 55.88) * mm, "end": v(-387.35, 55.88) * mm});
            skLineSegment(sketch, "E77", {"start": v(-387.35, 55.88) * mm, "end": v(-387.35, -147.32) * mm});
            skLineSegment(sketch, "E78", {"start": v(-387.35, -147.32) * mm, "end": v(-590.55, -147.32) * mm});
            skLineSegment(sketch, "E79", {"start": v(-590.55, -147.32) * mm, "end": v(-590.55, -340.66) * mm});
            skLineSegment(sketch, "E80", {"start": v(-590.55, -340.66) * mm, "end": v(-377.5, -340.66) * mm});
            skLineSegment(sketch, "E81", {"start": v(-377.5, -340.66) * mm, "end": v(19.05, 55.88) * mm});
            skLineSegment(sketch, "E82", {"start": v(19.05, 55.88) * mm, "end": v(19.05, 259.08) * mm});
            skLineSegment(sketch, "E83", {"start": v(-184.15, 55.88) * mm, "end": v(-82.55, -45.72) * mm, "construction": true});
            skLineSegment(sketch, "E84", {"start": v(-387.35, -147.32) * mm, "end": v(-285.75, -248.92) * mm, "construction": true});
            skSolve(sketch);
        }
        {
            var Q0;
            Q0 = qSketchRegion(id + "F54", true);
            extrude(context, id + "F55", {"entities" : qUnion([Q0]), "operationType" : NewBodyOperationType.ADD, "endBound" : BoundingType.SYMMETRIC, "depth" : 1219.2 * mm});
        }
        {
            var Q0;
            Q0=makeQuery(id+"F55.opExtrude","SWEPT_FACE",FACE,{"disambiguationData":[OSD([sQuery(id+"F54.wireOp",EDGE,"E79")])]});
            var sketch = newSketch(context, id + "F56", { "sketchPlane" : qUnion([Q0])});
            skLineSegment(sketch, "E85.bottom", {"start": v(1790.7, -340.66) * mm, "end": v(2146.3, -340.66) * mm});
            skLineSegment(sketch, "E85.top", {"start": v(1790.7, 259.08) * mm, "end": v(2146.3, 259.08) * mm});
            skLineSegment(sketch, "E85.left", {"start": v(1790.7, -340.66) * mm, "end": v(1790.7, 259.08) * mm});
            skLineSegment(sketch, "E85.right", {"start": v(2146.3, -340.66) * mm, "end": v(2146.3, 259.08) * mm});
            skLineSegment(sketch, "E86.bottom", {"start": v(2184.4, -340.66) * mm, "end": v(2540, -340.66) * mm});
            skLineSegment(sketch, "E86.top", {"start": v(2184.4, 259.08) * mm, "end": v(2540, 259.08) * mm});
            skLineSegment(sketch, "E86.left", {"start": v(2184.4, -340.66) * mm, "end": v(2184.4, 259.08) * mm});
            skLineSegment(sketch, "E86.right", {"start": v(2540, -340.66) * mm, "end": v(2540, 259.08) * mm});
            skLineSegment(sketch, "E87.bottom", {"start": v(2578.1, -340.66) * mm, "end": v(2933.7, -340.66) * mm});
            skLineSegment(sketch, "E87.top", {"start": v(2578.1, 259.08) * mm, "end": v(2933.7, 259.08) * mm});
            skLineSegment(sketch, "E87.left", {"start": v(2578.1, -340.66) * mm, "end": v(2578.1, 259.08) * mm});
            skLineSegment(sketch, "E87.right", {"start": v(2933.7, -340.66) * mm, "end": v(2933.7, 259.08) * mm});
            skSolve(sketch);
        }
        {
            var Q0;
            Q0 = qSketchRegion(id + "F56", true);
            var Q1;
            Q1=makeQuery(id+"F12.boolean.opBoolean","COPY",FACE,{"derivedFrom":makeQuery(id+"F12.opExtrude","CAP_FACE",FACE,{"disambiguationData":[OSD([sQuery(id+"F0.wireOp",EDGE,"E6"),sQuery(id+"F0.wireOp",EDGE,"E7"),sQuery(id+"F11.wireOp",EDGE,"E21"),sQuery(id+"F11.wireOp",EDGE,"E22"),sQuery(id+"F11.wireOp",EDGE,"E23")])],"isStart":false})});
            extrude(context, id + "F57", {"entities" : qUnion([Q0]), "operationType" : NewBodyOperationType.REMOVE, "endBound" : BoundingType.UP_TO_SURFACE, "oppositeDirection" : true, "endBoundEntityFace" : qUnion([Q1]), "depth" : 25.4 * mm});
        }
        {
            var Q0;
            Q0=makeQuery(id+"F55.opExtrude","CAP_FACE",FACE,{"disambiguationData":[OSD([sQuery(id+"F54.wireOp",EDGE,"E74"),sQuery(id+"F54.wireOp",EDGE,"E75"),sQuery(id+"F54.wireOp",EDGE,"E76"),sQuery(id+"F54.wireOp",EDGE,"E77"),sQuery(id+"F54.wireOp",EDGE,"E78"),sQuery(id+"F54.wireOp",EDGE,"E79"),sQuery(id+"F54.wireOp",EDGE,"E80"),sQuery(id+"F54.wireOp",EDGE,"E81"),sQuery(id+"F54.wireOp",EDGE,"E82")])],"isStart":false});
            var sketch = newSketch(context, id + "F58", { "sketchPlane" : qUnion([Q0])});
            skLineSegment(sketch, "E88.bottom", {"start": v(19.05, 259.08) * mm, "end": v(-222.25, 259.08) * mm});
            skLineSegment(sketch, "E88.top", {"start": v(19.05, 284.48) * mm, "end": v(-222.25, 284.48) * mm});
            skLineSegment(sketch, "E88.left", {"start": v(19.05, 259.08) * mm, "end": v(19.05, 284.48) * mm});
            skLineSegment(sketch, "E88.right", {"start": v(-222.25, 259.08) * mm, "end": v(-222.25, 284.48) * mm});
            skLineSegment(sketch, "E89.bottom", {"start": v(-184.15, 55.88) * mm, "end": v(-425.45, 55.88) * mm});
            skLineSegment(sketch, "E89.top", {"start": v(-184.15, 81.28) * mm, "end": v(-425.45, 81.28) * mm});
            skLineSegment(sketch, "E89.left", {"start": v(-184.15, 55.88) * mm, "end": v(-184.15, 81.28) * mm});
            skLineSegment(sketch, "E89.right", {"start": v(-425.45, 55.88) * mm, "end": v(-425.45, 81.28) * mm});
            skLineSegment(sketch, "E90.bottom", {"start": v(-387.35, -147.32) * mm, "end": v(-628.65, -147.32) * mm});
            skLineSegment(sketch, "E90.top", {"start": v(-387.35, -121.92) * mm, "end": v(-628.65, -121.92) * mm});
            skLineSegment(sketch, "E90.left", {"start": v(-387.35, -147.32) * mm, "end": v(-387.35, -121.92) * mm});
            skLineSegment(sketch, "E90.right", {"start": v(-628.65, -147.32) * mm, "end": v(-628.65, -121.92) * mm});
            skSolve(sketch);
        }
        {
            var Q0;
            Q0 = qSketchRegion(id + "F58", true);
            extrude(context, id + "F59", {"entities" : qUnion([Q0]), "operationType" : NewBodyOperationType.ADD, "depth" : 38.1 * mm, "hasSecondDirection" : true, "secondDirectionOppositeDirection" : true, "secondDirectionDepth" : 1257.3 * mm});
        }
        {
            var Q0;
            Q0=qCreatedBy(id+"F53.planeOp",FACE);
            var sketch = newSketch(context, id + "F60", { "sketchPlane" : qUnion([Q0])});
            skLineSegment(sketch, "E91.bottom", {"start": v(19.05, 292.1) * mm, "end": v(-44.45, 292.1) * mm});
            skLineSegment(sketch, "E91.top", {"start": v(19.05, 330.2) * mm, "end": v(-44.45, 330.2) * mm});
            skLineSegment(sketch, "E91.left", {"start": v(19.05, 292.1) * mm, "end": v(19.05, 330.2) * mm});
            skLineSegment(sketch, "E91.right", {"start": v(-44.45, 292.1) * mm, "end": v(-44.45, 330.2) * mm});
            skSolve(sketch);
        }
        {
            var Q0;
            Q0 = qSketchRegion(id + "F60", true);
            var Q1;
            Q1=makeQuery(id+"F59.opExtrude","CAP_FACE",FACE,{"disambiguationData":[OSD([sQuery(id+"F58.wireOp",EDGE,"E88.bottom"),sQuery(id+"F58.wireOp",EDGE,"E88.top"),sQuery(id+"F58.wireOp",EDGE,"E88.left"),sQuery(id+"F58.wireOp",EDGE,"E88.right")])],"isStart":false});
            var Q2;
            Q2=makeQuery(id+"F59.opExtrude","CAP_FACE",FACE,{"disambiguationData":[OSD([sQuery(id+"F58.wireOp",EDGE,"E88.bottom"),sQuery(id+"F58.wireOp",EDGE,"E88.top"),sQuery(id+"F58.wireOp",EDGE,"E88.left"),sQuery(id+"F58.wireOp",EDGE,"E88.right")])],"isStart":true});
            extrude(context, id + "F61", {"entities" : qUnion([Q0]), "operationType" : NewBodyOperationType.ADD, "endBound" : BoundingType.UP_TO_SURFACE, "endBoundEntityFace" : qUnion([Q1]), "depth" : 25.4 * mm, "hasSecondDirection" : true, "secondDirectionBound" : SecondDirectionBoundingType.UP_TO_SURFACE, "secondDirectionOppositeDirection" : true, "secondDirectionBoundEntityFace" : qUnion([Q2]), "secondDirectionDepth" : 25.4 * mm});
        }
        {
            var Q0;
            Q0=makeQuery(id+"F20.boolean.opBoolean","COPY",FACE,{"derivedFrom":makeQuery(id+"F20.opExtrude","SWEPT_FACE",FACE,{"disambiguationData":[OSD([sQuery(id+"F19.wireOp",EDGE,"E34.1")])]})});
            cPlane(context, id + "F62", {"entities" : qUnion([Q0]), "cplaneType" : CPlaneType.OFFSET, "offset" : 6.35 * mm, "width" : 152.4 * mm, "height" : 152.4 * mm});
        }
        {
            var Q0;
            Q0=qCreatedBy(id+"F62.planeOp",FACE);
            var sketch = newSketch(context, id + "F63", { "sketchPlane" : qUnion([Q0])});
            skLineSegment(sketch, "E92", {"start": v(3407.43, 2044.7) * mm, "end": v(3655.08, 1615.76) * mm});
            skLineSegment(sketch, "E93", {"start": v(3655.08, 1615.76) * mm, "end": v(3688.08, 1634.8) * mm});
            skLineSegment(sketch, "E94", {"start": v(3688.08, 1634.8) * mm, "end": v(3440.43, 2063.75) * mm});
            skLineSegment(sketch, "E95", {"start": v(3440.43, 2063.75) * mm, "end": v(3407.43, 2044.7) * mm});
            skSolve(sketch);
        }
        {
            var Q0;
            Q0 = qSketchRegion(id + "F63", true);
            extrude(context, id + "F64", {"entities" : qUnion([Q0]), "operationType" : NewBodyOperationType.ADD, "depth" : 647.7 * mm});
        }
        {
            var Q0;
            Q0=makeQuery(id+"F64.opExtrude","SWEPT_FACE",FACE,{"disambiguationData":[OSD([sQuery(id+"F63.wireOp",EDGE,"E94")])]});
            var sketch = newSketch(context, id + "F65", { "sketchPlane" : qUnion([Q0])});
            skLineSegment(sketch, "E96.0", {"start": v(1568.45, -377.46) * mm, "end": v(1568.45, 8.91) * mm});
            skLineSegment(sketch, "E96.1", {"start": v(1022.35, -377.46) * mm, "end": v(1568.45, -377.46) * mm});
            skLineSegment(sketch, "E96.2", {"start": v(1022.35, 8.91) * mm, "end": v(1022.35, -377.46) * mm});
            skLineSegment(sketch, "E96.3", {"start": v(1568.45, 8.91) * mm, "end": v(1022.35, 8.91) * mm});
            skSolve(sketch);
        }
        {
            var Q0;
            Q0 = qSketchRegion(id + "F65", true);
            extrude(context, id + "F66", {"entities" : qUnion([Q0]), "operationType" : NewBodyOperationType.REMOVE, "oppositeDirection" : true, "depth" : 19.05 * mm});
        }
        {
            var Q0;
            Q0=makeQuery(id+"F1.opExtrude","SWEPT_FACE",FACE,{"disambiguationData":[OSD([sQuery(id+"F0.wireOp",EDGE,"E6")])]});
            var sketch = newSketch(context, id + "F67", { "sketchPlane" : qUnion([Q0])});
            skPoint(sketch, "E97.firstSnap0", {"position": v(152.4, -63.5) * mm});
            skLineSegment(sketch, "E97.bottom", {"start": v(209.55, -63.5) * mm, "end": v(336.55, -63.5) * mm});
            skLineSegment(sketch, "E97.top", {"start": v(209.55, -190.5) * mm, "end": v(336.55, -190.5) * mm});
            skLineSegment(sketch, "E97.left", {"start": v(209.55, -63.5) * mm, "end": v(209.55, -190.5) * mm});
            skLineSegment(sketch, "E97.right", {"start": v(336.55, -63.5) * mm, "end": v(336.55, -190.5) * mm});
            skLineSegment(sketch, "E98.bottom", {"start": v(1707.65, -63.5) * mm, "end": v(1834.65, -63.5) * mm});
            skLineSegment(sketch, "E98.top", {"start": v(1707.65, -186.72) * mm, "end": v(1834.65, -186.72) * mm});
            skLineSegment(sketch, "E98.left", {"start": v(1707.65, -63.5) * mm, "end": v(1707.65, -186.72) * mm});
            skLineSegment(sketch, "E98.right", {"start": v(1834.65, -63.5) * mm, "end": v(1834.65, -186.72) * mm});
            skPoint(sketch, "E99.firstSnap0", {"position": v(3479.8, -63.5) * mm});
            skLineSegment(sketch, "E99.bottom", {"start": v(3295.65, -63.5) * mm, "end": v(3422.65, -63.5) * mm});
            skLineSegment(sketch, "E99.top", {"start": v(3295.65, -186.72) * mm, "end": v(3422.65, -186.72) * mm});
            skLineSegment(sketch, "E99.left", {"start": v(3295.65, -63.5) * mm, "end": v(3295.65, -186.72) * mm});
            skLineSegment(sketch, "E99.right", {"start": v(3422.65, -63.5) * mm, "end": v(3422.65, -186.72) * mm});
            skPoint(sketch, "E100.firstSnap0", {"position": v(3416.3, -2438.4) * mm});
            skLineSegment(sketch, "E100.bottom", {"start": v(3416.3, -2379.02) * mm, "end": v(3289.3, -2379.02) * mm});
            skLineSegment(sketch, "E100.top", {"start": v(3416.3, -2252.02) * mm, "end": v(3289.3, -2252.02) * mm});
            skLineSegment(sketch, "E100.left", {"start": v(3416.3, -2379.02) * mm, "end": v(3416.3, -2252.02) * mm});
            skLineSegment(sketch, "E100.right", {"start": v(3289.3, -2379.02) * mm, "end": v(3289.3, -2252.02) * mm});
            skLineSegment(sketch, "E101.bottom", {"start": v(1722.59, -2379.02) * mm, "end": v(1849.59, -2379.02) * mm});
            skLineSegment(sketch, "E101.top", {"start": v(1722.59, -2252.02) * mm, "end": v(1849.59, -2252.02) * mm});
            skLineSegment(sketch, "E101.left", {"start": v(1722.59, -2379.02) * mm, "end": v(1722.59, -2252.02) * mm});
            skLineSegment(sketch, "E101.right", {"start": v(1849.59, -2379.02) * mm, "end": v(1849.59, -2252.02) * mm});
            skLineSegment(sketch, "E102.bottom", {"start": v(209.55, -2379.02) * mm, "end": v(336.55, -2379.02) * mm});
            skLineSegment(sketch, "E102.top", {"start": v(209.55, -2252.02) * mm, "end": v(336.55, -2252.02) * mm});
            skLineSegment(sketch, "E102.left", {"start": v(209.55, -2379.02) * mm, "end": v(209.55, -2252.02) * mm});
            skLineSegment(sketch, "E102.right", {"start": v(336.55, -2379.02) * mm, "end": v(336.55, -2252.02) * mm});
            skSolve(sketch);
        }
        {
            var Q0;
            Q0 = qSketchRegion(id + "F67", true);
            extrude(context, id + "F68", {"entities" : qUnion([Q0]), "operationType" : NewBodyOperationType.ADD, "depth" : 508 * mm});
        }
    });
